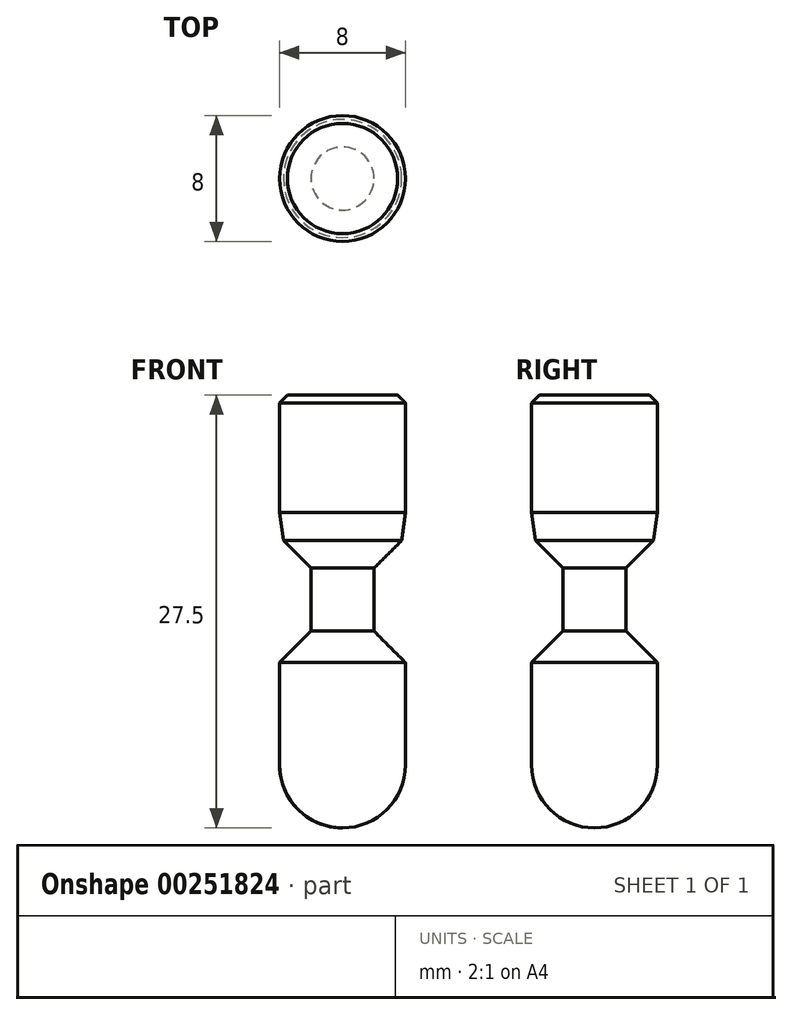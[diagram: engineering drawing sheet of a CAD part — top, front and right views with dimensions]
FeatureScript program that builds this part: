
annotation { "Feature Type Name" : "Feature", "Feature Type Description" : "" }
export const myFeature = defineFeature(function(context is Context, id is Id, definition is map)
    precondition{}
    {
        {
            var Q0;
            Q0=qCreatedBy(makeId("Front.planeOp"),FACE);
            var sketch = newSketch(context, id + "F0", { "sketchPlane" : qUnion([Q0])});
            skLineSegment(sketch, "E0", {"start": v(0, 15) * mm, "end": v(0, -12.5) * mm});
            skLineSegment(sketch, "E1", {"start": v(-4, -8.5) * mm, "end": v(0, -8.5) * mm});
            skArc(sketch, "E2", {"start": v(-4, -8.5) * mm, "mid": v(-2.83, -11.33) * mm, "end": v(0, -12.5) * mm});
            skLineSegment(sketch, "E3", {"start": v(-4, -8.5) * mm, "end": v(-4, -2) * mm});
            skLineSegment(sketch, "E4", {"start": v(-4, -2) * mm, "end": v(0, -2) * mm});
            skLineSegment(sketch, "E5", {"start": v(-4, -2) * mm, "end": v(-2, 0) * mm});
            skLineSegment(sketch, "E6", {"start": v(-2, 0) * mm, "end": v(0, 0) * mm});
            skLineSegment(sketch, "E7", {"start": v(-2, 0) * mm, "end": v(-2, 4) * mm});
            skLineSegment(sketch, "E8", {"start": v(-2, 4) * mm, "end": v(-3.75, 5.75) * mm});
            skLineSegment(sketch, "E9", {"start": v(-3.75, 5.75) * mm, "end": v(0, 5.75) * mm});
            skLineSegment(sketch, "E10", {"start": v(0, 5.75) * mm, "end": v(0, 4) * mm});
            skLineSegment(sketch, "E11", {"start": v(0, 4) * mm, "end": v(-2, 4) * mm});
            skLineSegment(sketch, "E12", {"start": v(-3.75, 5.75) * mm, "end": v(-4, 7.53) * mm});
            skLineSegment(sketch, "E13", {"start": v(-4, 7.53) * mm, "end": v(0, 7.53) * mm});
            skLineSegment(sketch, "E14", {"start": v(-4, 7.53) * mm, "end": v(-4, 15) * mm});
            skLineSegment(sketch, "E15", {"start": v(0, 15) * mm, "end": v(0, 15) * mm});
            skLineSegment(sketch, "E16", {"start": v(0, 15) * mm, "end": v(-4, 15) * mm});
            skLineSegment(sketch, "E17", {"start": v(-4, 15) * mm, "end": v(-4, 15) * mm});
            skLineSegment(sketch, "E18", {"start": v(-3.75, 5.75) * mm, "end": v(-4.76, 12.96) * mm, "construction": true});
            skSolve(sketch);
        }
        {
            var Q0;
            Q0 = qSketchRegion(id + "F0", true);
            var Q1;
            Q1=sQuery(id+"F0.wireOp",EDGE,"E0");
            revolve(context, id + "F1", {"entities" : qUnion([Q0]), "axis" : qUnion([Q1]), "revolveType" : RevolveType.FULL});
        }
        {
            var Q0;
            Q0=makeQuery(id+"F1.opRevolve","SWEPT_EDGE",EDGE,{"disambiguationData":[OSD([sQuery(id+"F0.wireOp",EDGE,"E14"),sQuery(id+"F0.wireOp",EDGE,"E16")])]});
            chamfer(context, id + "F2", {"entities" : qUnion([Q0]), "chamferType" : ChamferType.OFFSET_ANGLE, "width" : .5 * mm, "oppositeDirection" : false, "angle" : 45 * degree, "tangentPropagation" : true});
        }
    });
